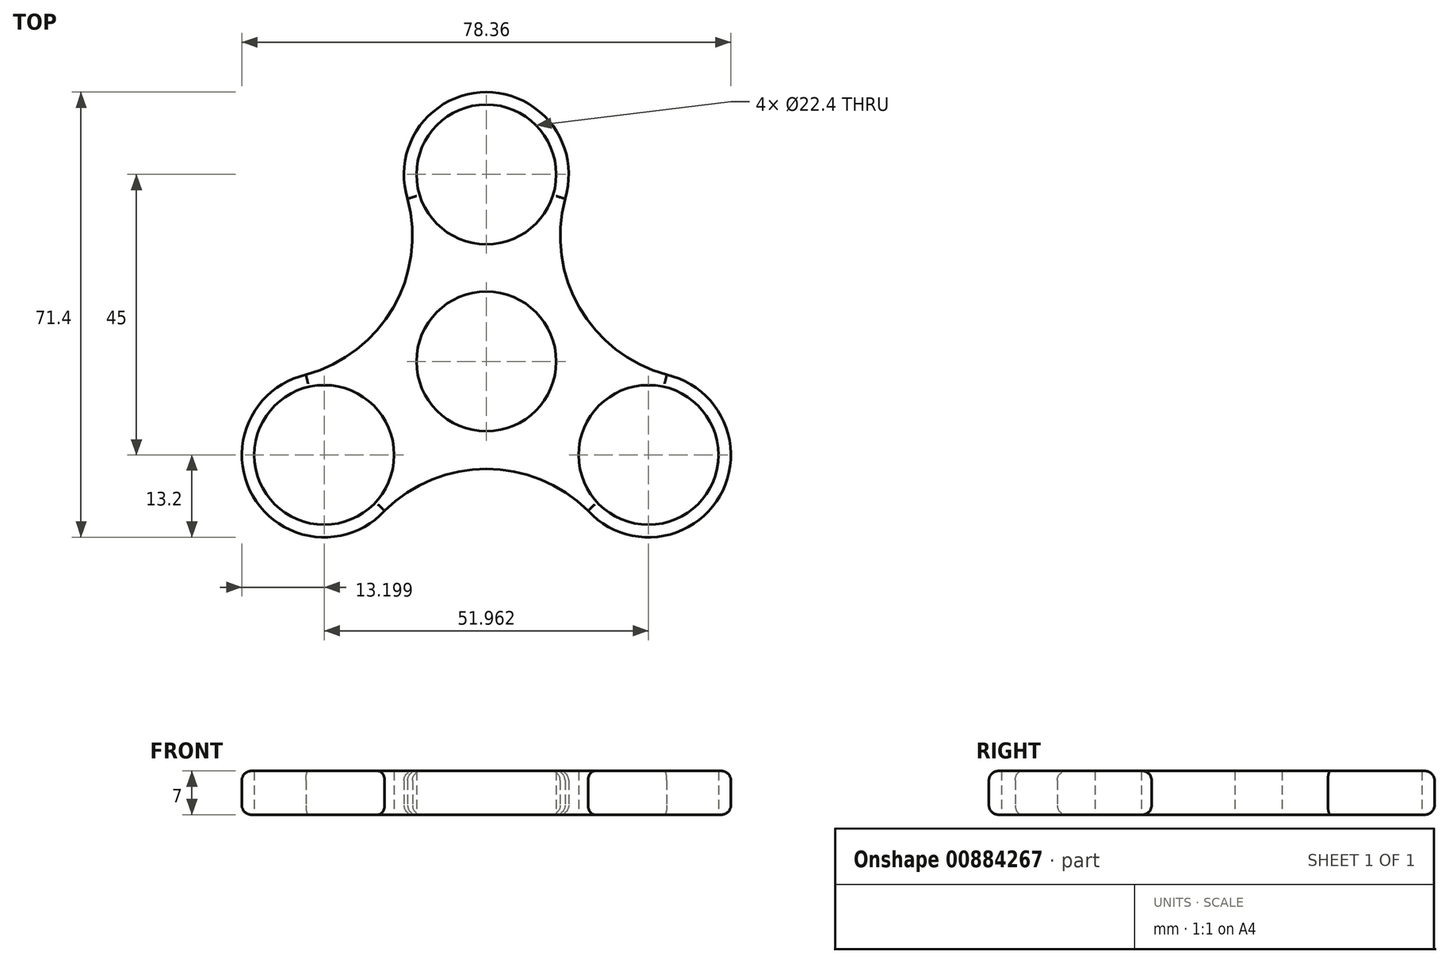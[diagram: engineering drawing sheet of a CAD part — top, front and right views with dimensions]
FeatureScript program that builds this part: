
annotation { "Feature Type Name" : "Feature", "Feature Type Description" : "" }
export const myFeature = defineFeature(function(context is Context, id is Id, definition is map)
    precondition{}
    {
        {
            var Q0;
            Q0=qCreatedBy(makeId("Top.planeOp"),FACE);
            var sketch = newSketch(context, id + "F0", { "sketchPlane" : qUnion([Q0])});
            skCircle(sketch, "E0", {"center": v(0, 0) * mm, "radius": 11.2 * mm});
            skCircle(sketch, "E1", {"center": v(0, 30) * mm, "radius": 11.2 * mm});
            skArc(sketch, "E2", {"start": v(12.61, 26.1) * mm, "mid": v(0, 43.2) * mm, "end": v(-12.61, 26.1) * mm});
            skArc(sketch, "E3.1.0", {"start": v(-28.92, -2.13) * mm, "mid": v(-37.41, -21.6) * mm, "end": v(-16.3, -23.98) * mm});
            skArc(sketch, "E3.2.0", {"start": v(16.3, -23.98) * mm, "mid": v(37.41, -21.6) * mm, "end": v(28.92, -2.13) * mm});
            skLineSegment(sketch, "E4", {"start": v(12.61, 26.1) * mm, "end": v(28.92, -2.13) * mm, "construction": true});
            skArc(sketch, "E5", {"start": v(12.61, 26.1) * mm, "mid": v(14.94, 8.62) * mm, "end": v(28.92, -2.13) * mm});
            skArc(sketch, "E6.1.0", {"start": v(-28.92, -2.13) * mm, "mid": v(-14.94, 8.62) * mm, "end": v(-12.61, 26.1) * mm});
            skArc(sketch, "E6.2.0", {"start": v(16.3, -23.98) * mm, "mid": v(0, -17.25) * mm, "end": v(-16.3, -23.98) * mm});
            skCircle(sketch, "E7.1.0", {"center": v(-25.98, -15) * mm, "radius": 11.2 * mm});
            skCircle(sketch, "E7.2.0", {"center": v(25.98, -15) * mm, "radius": 11.2 * mm});
            skPoint(sketch, "E8.trimOffspring.end.orphan", {"position": v(25.98, 15) * mm});
            skSolve(sketch);
        }
        {
            var Q0;
            Q0 = qSketchRegion(id + "F0", true);
            extrude(context, id + "F1", {"entities" : qUnion([Q0]), "depth" : 7 * mm, "offsetDistance" : 25 * mm});
        }
        {
            var Q0;
            Q0=makeQuery(id+"F1.opExtrude","CAP_EDGE",EDGE,{"disambiguationData":[OSD([sQuery(id+"F0.wireOp",EDGE,"E6.2.0")])],"isStart":false});
            var Q1;
            Q1=makeQuery(id+"F1.opExtrude","CAP_EDGE",EDGE,{"disambiguationData":[OSD([sQuery(id+"F0.wireOp",EDGE,"E3.2.0")])],"isStart":false});
            var Q2;
            Q2=makeQuery(id+"F1.opExtrude","CAP_EDGE",EDGE,{"disambiguationData":[OSD([sQuery(id+"F0.wireOp",EDGE,"E5")])],"isStart":false});
            var Q3;
            Q3=makeQuery(id+"F1.opExtrude","CAP_EDGE",EDGE,{"disambiguationData":[OSD([sQuery(id+"F0.wireOp",EDGE,"E2")])],"isStart":false});
            var Q4;
            Q4=makeQuery(id+"F1.opExtrude","CAP_EDGE",EDGE,{"disambiguationData":[OSD([sQuery(id+"F0.wireOp",EDGE,"E6.1.0")])],"isStart":false});
            var Q5;
            Q5=makeQuery(id+"F1.opExtrude","CAP_EDGE",EDGE,{"disambiguationData":[OSD([sQuery(id+"F0.wireOp",EDGE,"E3.1.0")])],"isStart":false});
            var Q6;
            Q6=makeQuery(id+"F1.opExtrude","CAP_EDGE",EDGE,{"disambiguationData":[OSD([sQuery(id+"F0.wireOp",EDGE,"E3.2.0")])],"isStart":true});
            var Q7;
            Q7=makeQuery(id+"F1.opExtrude","CAP_EDGE",EDGE,{"disambiguationData":[OSD([sQuery(id+"F0.wireOp",EDGE,"E2")])],"isStart":true});
            var Q8;
            Q8=makeQuery(id+"F1.opExtrude","CAP_EDGE",EDGE,{"disambiguationData":[OSD([sQuery(id+"F0.wireOp",EDGE,"E5")])],"isStart":true});
            var Q9;
            Q9=makeQuery(id+"F1.opExtrude","CAP_EDGE",EDGE,{"disambiguationData":[OSD([sQuery(id+"F0.wireOp",EDGE,"E6.1.0")])],"isStart":true});
            var Q10;
            Q10=makeQuery(id+"F1.opExtrude","CAP_EDGE",EDGE,{"disambiguationData":[OSD([sQuery(id+"F0.wireOp",EDGE,"E3.1.0")])],"isStart":true});
            fillet(context, id + "F2", {"entities" : qUnion([Q0, Q1, Q2, Q3, Q4, Q5, Q6, Q7, Q8, Q9, Q10]), "radius" : 1.5 * mm, "tangentPropagation" : true, "allowEdgeOverflow" : false});
        }
    });
